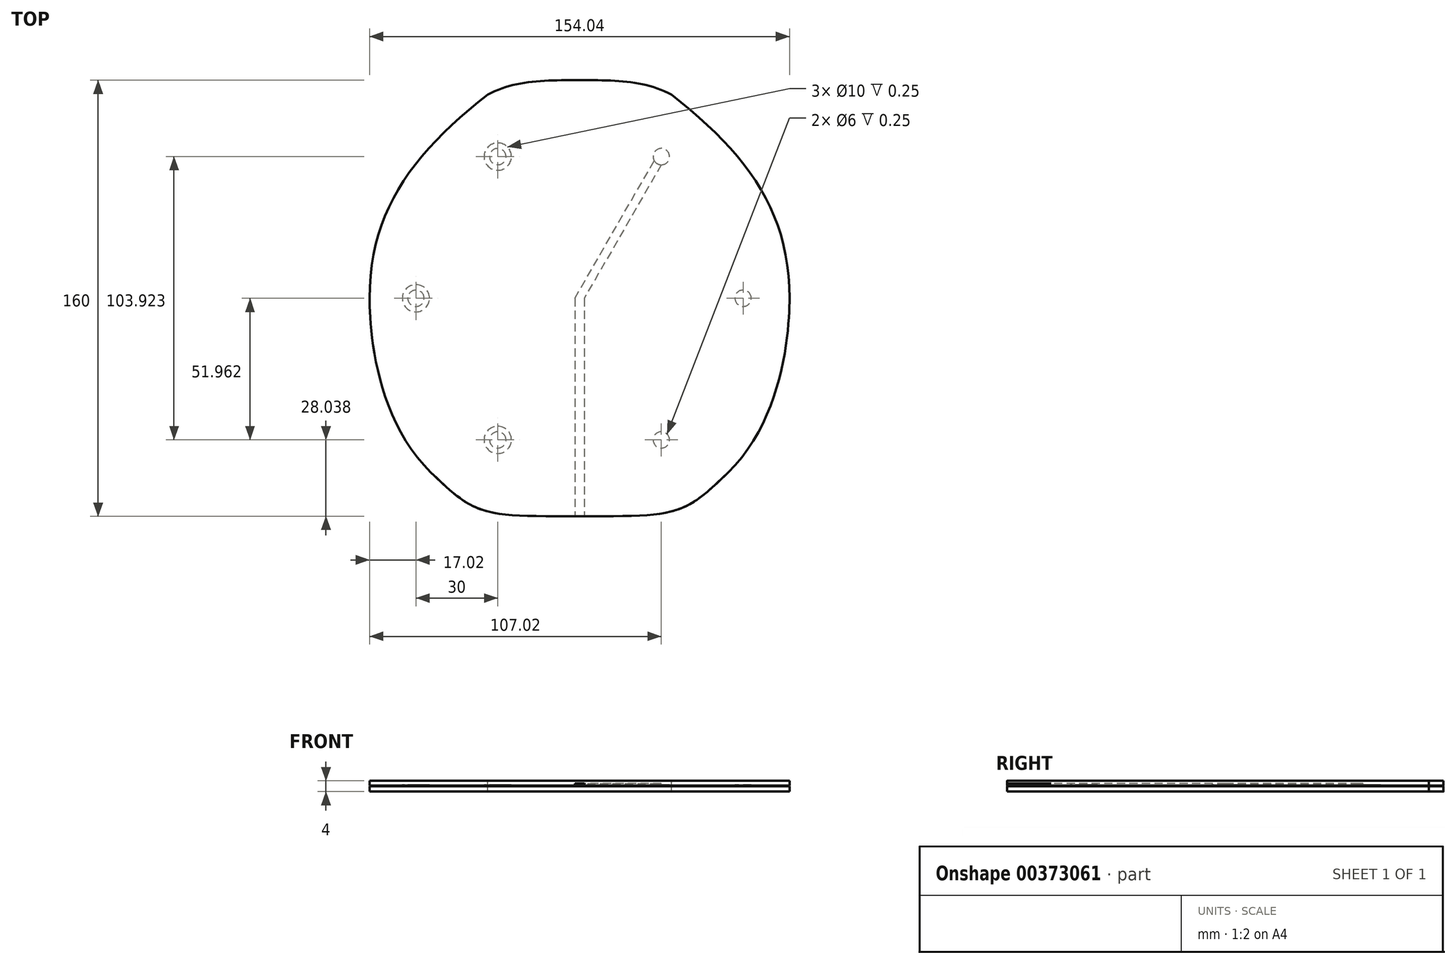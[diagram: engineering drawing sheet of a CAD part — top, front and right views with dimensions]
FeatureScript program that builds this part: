
annotation { "Feature Type Name" : "Feature", "Feature Type Description" : "" }
export const myFeature = defineFeature(function(context is Context, id is Id, definition is map)
    precondition{}
    {
        {
            assignVariable(context, id + "F0", {"name" : "spacer_thickness", "anyValue" : 2});
        }
        {
            var Q0;
            Q0=qCreatedBy(makeId("Top.planeOp"),FACE);
            var sketch = newSketch(context, id + "F1", { "sketchPlane" : qUnion([Q0])});
            skLineSegment(sketch, "E0", {"start": v(0, 80) * mm, "end": v(0, -80) * mm, "construction": true});
            skLineSegment(sketch, "E1", {"start": v(-77.02, 0) * mm, "end": v(77.02, 0) * mm, "construction": true});
            skFitSpline(sketch, "E2", {"points": [v(0, -80) * mm, v(-54.47, -63.95) * mm], "startDerivative": vector(-107.49, 0) * mm, "endDerivative": vector(-49.64, 48.15) * mm});
            skFitSpline(sketch, "E3", {"points": [v(-54.47, -63.95) * mm, v(-77.02, 0) * mm], "startDerivative": vector(-62.84, 60.95) * mm, "endDerivative": vector(0, 29.3) * mm});
            skFitSpline(sketch, "E4", {"points": [v(-77.02, 0) * mm, v(-33.74, 74.65) * mm], "startDerivative": vector(0, 97.25) * mm, "endDerivative": vector(81.5, 63.98) * mm});
            skFitSpline(sketch, "E5", {"points": [v(-33.74, 74.65) * mm, v(0, 80) * mm], "startDerivative": vector(30.02, 16.04) * mm, "endDerivative": vector(39.73, 0) * mm});
            skFitSpline(sketch, "E6.MirrorCS", {"points": [v(33.74, 74.65) * mm, v(0, 80) * mm], "startDerivative": vector(-30.02, 16.04) * mm, "endDerivative": vector(-39.73, 0) * mm});
            skFitSpline(sketch, "E7.MirrorCS", {"points": [v(77.02, 0) * mm, v(33.74, 74.65) * mm], "startDerivative": vector(0, 97.25) * mm, "endDerivative": vector(-81.5, 63.98) * mm});
            skFitSpline(sketch, "E8.MirrorCS", {"points": [v(54.47, -63.95) * mm, v(77.02, 0) * mm], "startDerivative": vector(62.84, 60.95) * mm, "endDerivative": vector(0, 29.3) * mm});
            skFitSpline(sketch, "E9.MirrorCS", {"points": [v(0, -80) * mm, v(54.47, -63.95) * mm], "startDerivative": vector(107.49, 0) * mm, "endDerivative": vector(49.64, 48.15) * mm});
            skSolve(sketch);
        }
        {
            var Q0;
            Q0=makeQuery(id+"F1.imprint","IMPRINT",FACE,{"disambiguationData":[TD([[makeQuery(id+"F1.imprint","IMPRINT",EDGE,{"derivedFrom":sQuery(id+"F1.wireOp",EDGE,"E2")}),-1.0]])]});
            extrude(context, id + "F2", {"entities" : qUnion([Q0]), "depth" : (getVariable(context, 'spacer_thickness')) * mm});
        }
        {
            assignVariable(context, id + "F3", {"name" : "wire_channel", "anyValue" : 1});
        }
        {
            assignVariable(context, id + "F4", {"name" : "piezo_thickness", "anyValue" : 0.5});
        }
        {
            assignVariable(context, id + "F5", {"name" : "piezo_plate_thickness", "anyValue" : 0.25});
        }
        {
            assignVariable(context, id + "F6", {"name" : "spacer_bottom_thickness", "anyValue" : 2});
        }
        {
            var Q0;
            Q0=makeQuery(id+"F2.opExtrude","CAP_FACE",FACE,{"disambiguationData":[OSD([sQuery(id+"F1.wireOp",EDGE,"E2"),sQuery(id+"F1.wireOp",EDGE,"E3"),sQuery(id+"F1.wireOp",EDGE,"E4"),sQuery(id+"F1.wireOp",EDGE,"E5"),sQuery(id+"F1.wireOp",EDGE,"E6.MirrorCS"),sQuery(id+"F1.wireOp",EDGE,"E7.MirrorCS"),sQuery(id+"F1.wireOp",EDGE,"E8.MirrorCS"),sQuery(id+"F1.wireOp",EDGE,"E9.MirrorCS")])],"isStart":false});
            var sketch = newSketch(context, id + "F7", { "sketchPlane" : qUnion([Q0])});
            skCircle(sketch, "E10", {"center": v(30, 51.96) * mm, "radius": 5 * mm});
            skCircle(sketch, "E11", {"center": v(60, 0) * mm, "radius": 5 * mm});
            skCircle(sketch, "E12", {"center": v(30, -51.96) * mm, "radius": 5 * mm});
            skCircle(sketch, "E13", {"center": v(0, 0) * mm, "radius": 60 * mm, "construction": true});
            skLineSegment(sketch, "E14", {"start": v(-119.63, 0) * mm, "end": v(92.07, 0) * mm, "construction": true});
            skLineSegment(sketch, "E15", {"start": v(0, 0) * mm, "end": v(44.3, 76.73) * mm, "construction": true});
            skCircle(sketch, "E16.MirrorC", {"center": v(-30, 51.96) * mm, "radius": 5 * mm});
            skCircle(sketch, "E17.MirrorC", {"center": v(-60, 0) * mm, "radius": 5 * mm});
            skCircle(sketch, "E18.MirrorC", {"center": v(-30, -51.96) * mm, "radius": 5 * mm});
            skCircle(sketch, "E19", {"center": v(30, 51.96) * mm, "radius": 3 * mm});
            skCircle(sketch, "E20", {"center": v(60, 0) * mm, "radius": 3 * mm});
            skCircle(sketch, "E21", {"center": v(30, -51.96) * mm, "radius": 3 * mm});
            skCircle(sketch, "E22.MirrorC", {"center": v(-60, 0) * mm, "radius": 3 * mm});
            skCircle(sketch, "E23.MirrorC", {"center": v(-30, 51.96) * mm, "radius": 3 * mm});
            skCircle(sketch, "E24.MirrorC", {"center": v(-30, -51.96) * mm, "radius": 3 * mm});
            skLineSegment(sketch, "E25", {"start": v(-1.73, 0) * mm, "end": v(28.2, 51.83) * mm});
            skLineSegment(sketch, "E26", {"start": v(29.56, 52.2) * mm, "end": v(30.42, 51.7) * mm});
            skLineSegment(sketch, "E27", {"start": v(30.79, 50.33) * mm, "end": v(1.73, 0) * mm});
            skLineSegment(sketch, "E28.bottom", {"start": v(-1.73, 0) * mm, "end": v(1.73, 0) * mm});
            skLineSegment(sketch, "E28.top", {"start": v(-1.73, -80) * mm, "end": v(1.73, -80) * mm});
            skLineSegment(sketch, "E28.left", {"start": v(-1.73, 0) * mm, "end": v(-1.73, -80) * mm});
            skLineSegment(sketch, "E28.right", {"start": v(1.73, 0) * mm, "end": v(1.73, -80) * mm});
            skPoint(sketch, "E29.visualSharp", {"position": v(28.7, 52.7) * mm});
            skArc(sketch, "E29.filletArc", {"start": v(29.56, 52.2) * mm, "mid": v(28.8, 52.3) * mm, "end": v(28.2, 51.83) * mm});
            skPoint(sketch, "E30.visualSharp", {"position": v(31.29, 51.2) * mm});
            skArc(sketch, "E30.filletArc", {"start": v(30.79, 50.33) * mm, "mid": v(30.89, 51.09) * mm, "end": v(30.42, 51.7) * mm});
            skSolve(sketch);
        }
        {
            var Q0;
            Q0=makeQuery(id+"F7.imprint","IMPRINT",FACE,{"disambiguationData":[TD([[makeQuery(id+"F7.imprint","IMPRINT",EDGE,{"derivedFrom":sQuery(id+"F7.wireOp",EDGE,"E10")}),1.0]])]});
            var Q1;
            Q1=makeQuery(id+"F7.imprint","IMPRINT",FACE,{"disambiguationData":[TD([[makeQuery(id+"F7.imprint","IMPRINT",EDGE,{"derivedFrom":sQuery(id+"F7.wireOp",EDGE,"E19")}),1.0]])]});
            var Q2;
            Q2=makeQuery(id+"F7.imprint","IMPRINT",FACE,{"disambiguationData":[TD([[makeQuery(id+"F7.imprint","IMPRINT",EDGE,{"derivedFrom":sQuery(id+"F7.wireOp",EDGE,"E11")}),1.0]])]});
            var Q3;
            Q3=makeQuery(id+"F7.imprint","IMPRINT",FACE,{"disambiguationData":[TD([[makeQuery(id+"F7.imprint","IMPRINT",EDGE,{"derivedFrom":sQuery(id+"F7.wireOp",EDGE,"E20")}),1.0]])]});
            var Q4;
            Q4=makeQuery(id+"F7.imprint","IMPRINT",FACE,{"disambiguationData":[TD([[makeQuery(id+"F7.imprint","IMPRINT",EDGE,{"derivedFrom":sQuery(id+"F7.wireOp",EDGE,"E12")}),1.0]])]});
            var Q5;
            Q5=makeQuery(id+"F7.imprint","IMPRINT",FACE,{"disambiguationData":[TD([[makeQuery(id+"F7.imprint","IMPRINT",EDGE,{"derivedFrom":sQuery(id+"F7.wireOp",EDGE,"E21")}),1.0]])]});
            var Q6;
            Q6=makeQuery(id+"F7.imprint","IMPRINT",FACE,{"disambiguationData":[TD([[makeQuery(id+"F7.imprint","IMPRINT",EDGE,{"derivedFrom":sQuery(id+"F7.wireOp",EDGE,"E18.MirrorC")}),-1.0]])]});
            var Q7;
            Q7=makeQuery(id+"F7.imprint","IMPRINT",FACE,{"disambiguationData":[TD([[makeQuery(id+"F7.imprint","IMPRINT",EDGE,{"derivedFrom":sQuery(id+"F7.wireOp",EDGE,"E24.MirrorC")}),-1.0]])]});
            var Q8;
            Q8=makeQuery(id+"F7.imprint","IMPRINT",FACE,{"disambiguationData":[TD([[makeQuery(id+"F7.imprint","IMPRINT",EDGE,{"derivedFrom":sQuery(id+"F7.wireOp",EDGE,"E17.MirrorC")}),-1.0]])]});
            var Q9;
            Q9=makeQuery(id+"F7.imprint","IMPRINT",FACE,{"disambiguationData":[TD([[makeQuery(id+"F7.imprint","IMPRINT",EDGE,{"derivedFrom":sQuery(id+"F7.wireOp",EDGE,"E22.MirrorC")}),-1.0]])]});
            var Q10;
            Q10=makeQuery(id+"F7.imprint","IMPRINT",FACE,{"disambiguationData":[TD([[makeQuery(id+"F7.imprint","IMPRINT",EDGE,{"derivedFrom":sQuery(id+"F7.wireOp",EDGE,"E16.MirrorC")}),-1.0]])]});
            var Q11;
            Q11=makeQuery(id+"F7.imprint","IMPRINT",FACE,{"disambiguationData":[TD([[makeQuery(id+"F7.imprint","IMPRINT",EDGE,{"derivedFrom":sQuery(id+"F7.wireOp",EDGE,"E23.MirrorC")}),-1.0]])]});
            var Q12;
            Q12=makeQuery(id+"F7.imprint","IMPRINT",FACE,{"disambiguationData":[TD([[makeQuery(id+"F7.imprint","IMPRINT",EDGE,{"derivedFrom":sQuery(id+"F7.wireOp",EDGE,"E19")}),-1.0]])]});
            var Q13;
            Q13=makeQuery(id+"F2.opExtrude","SWEPT_BODY",BODY,{"disambiguationData":[OSD([sQuery(id+"F1.wireOp",EDGE,"E2"),sQuery(id+"F1.wireOp",EDGE,"E3"),sQuery(id+"F1.wireOp",EDGE,"E4"),sQuery(id+"F1.wireOp",EDGE,"E5"),sQuery(id+"F1.wireOp",EDGE,"E6.MirrorCS"),sQuery(id+"F1.wireOp",EDGE,"E7.MirrorCS"),sQuery(id+"F1.wireOp",EDGE,"E8.MirrorCS"),sQuery(id+"F1.wireOp",EDGE,"E9.MirrorCS")])]});
            extrude(context, id + "F8", {"entities" : qUnion([Q0, Q1, Q2, Q3, Q4, Q5, Q6, Q7, Q8, Q9, Q10, Q11, Q12]), "operationType" : NewBodyOperationType.REMOVE, "oppositeDirection" : true, "endBoundEntityBody" : qUnion([Q13]), "depth" : (getVariable(context, 'spacer_thickness')) * mm});
        }
        {
            var Q0;
            Q0=makeQuery(id+"F7.imprint","IMPRINT",FACE,{"disambiguationData":[TD([[makeQuery(id+"F7.imprint","IMPRINT",EDGE,{"derivedFrom":sQuery(id+"F7.wireOp",EDGE,"E10")}),1.0]])]});
            var Q1;
            Q1=makeQuery(id+"F7.imprint","IMPRINT",FACE,{"disambiguationData":[TD([[makeQuery(id+"F7.imprint","IMPRINT",EDGE,{"derivedFrom":sQuery(id+"F7.wireOp",EDGE,"E11")}),1.0]])]});
            var Q2;
            Q2=makeQuery(id+"F7.imprint","IMPRINT",FACE,{"disambiguationData":[TD([[makeQuery(id+"F7.imprint","IMPRINT",EDGE,{"derivedFrom":sQuery(id+"F7.wireOp",EDGE,"E12")}),1.0]])]});
            var Q3;
            Q3=makeQuery(id+"F7.imprint","IMPRINT",FACE,{"disambiguationData":[TD([[makeQuery(id+"F7.imprint","IMPRINT",EDGE,{"derivedFrom":sQuery(id+"F7.wireOp",EDGE,"E18.MirrorC")}),-1.0]])]});
            var Q4;
            Q4=makeQuery(id+"F7.imprint","IMPRINT",FACE,{"disambiguationData":[TD([[makeQuery(id+"F7.imprint","IMPRINT",EDGE,{"derivedFrom":sQuery(id+"F7.wireOp",EDGE,"E17.MirrorC")}),-1.0]])]});
            var Q5;
            Q5=makeQuery(id+"F7.imprint","IMPRINT",FACE,{"disambiguationData":[TD([[makeQuery(id+"F7.imprint","IMPRINT",EDGE,{"derivedFrom":sQuery(id+"F7.wireOp",EDGE,"E16.MirrorC")}),-1.0]])]});
            var Q6;
            Q6=makeQuery(id+"F7.imprint","IMPRINT",FACE,{"disambiguationData":[TD([[makeQuery(id+"F7.imprint","IMPRINT",EDGE,{"derivedFrom":sQuery(id+"F7.wireOp",EDGE,"E19")}),-1.0]])]});
            extrude(context, id + "F9", {"entities" : qUnion([Q0, Q1, Q2, Q3, Q4, Q5, Q6]), "operationType" : NewBodyOperationType.ADD, "oppositeDirection" : true, "depth" : (getVariable(context, 'spacer_thickness') - getVariable(context, 'piezo_plate_thickness')) * mm});
        }
        {
            var Q0;
            Q0=makeQuery(id+"F7.imprint","IMPRINT",FACE,{"disambiguationData":[TD([[makeQuery(id+"F7.imprint","IMPRINT",EDGE,{"derivedFrom":sQuery(id+"F7.wireOp",EDGE,"E19")}),1.0]])]});
            var Q1;
            Q1=makeQuery(id+"F7.imprint","IMPRINT",FACE,{"disambiguationData":[TD([[makeQuery(id+"F7.imprint","IMPRINT",EDGE,{"derivedFrom":sQuery(id+"F7.wireOp",EDGE,"E20")}),1.0]])]});
            var Q2;
            Q2=makeQuery(id+"F7.imprint","IMPRINT",FACE,{"disambiguationData":[TD([[makeQuery(id+"F7.imprint","IMPRINT",EDGE,{"derivedFrom":sQuery(id+"F7.wireOp",EDGE,"E21")}),1.0]])]});
            var Q3;
            Q3=makeQuery(id+"F7.imprint","IMPRINT",FACE,{"disambiguationData":[TD([[makeQuery(id+"F7.imprint","IMPRINT",EDGE,{"derivedFrom":sQuery(id+"F7.wireOp",EDGE,"E24.MirrorC")}),-1.0]])]});
            var Q4;
            Q4=makeQuery(id+"F7.imprint","IMPRINT",FACE,{"disambiguationData":[TD([[makeQuery(id+"F7.imprint","IMPRINT",EDGE,{"derivedFrom":sQuery(id+"F7.wireOp",EDGE,"E22.MirrorC")}),-1.0]])]});
            var Q5;
            Q5=makeQuery(id+"F7.imprint","IMPRINT",FACE,{"disambiguationData":[TD([[makeQuery(id+"F7.imprint","IMPRINT",EDGE,{"derivedFrom":sQuery(id+"F7.wireOp",EDGE,"E23.MirrorC")}),-1.0]])]});
            extrude(context, id + "F10", {"entities" : qUnion([Q0, Q1, Q2, Q3, Q4, Q5]), "operationType" : NewBodyOperationType.ADD, "oppositeDirection" : true, "depth" : (getVariable(context, 'spacer_thickness') - getVariable(context, 'piezo_thickness')) * mm});
        }
        {
            var Q0;
            {var subQ1=sQuery(id+"F7.wireOp",EDGE,"E25");Q0=makeQuery(id+"F7.imprint","IMPRINT",FACE,{"disambiguationData":[TD([[makeQuery(id+"F7.imprint","IMPRINT",EDGE,{"derivedFrom":subQ1}),-1.0]])]});}
            extrude(context, id + "F11", {"entities" : qUnion([Q0]), "operationType" : NewBodyOperationType.REMOVE, "oppositeDirection" : true, "depth" : 5 * mm});
        }
        {
            var Q0;
            {var subQ1=sQuery(id+"F7.wireOp",EDGE,"E25");Q0=makeQuery(id+"F7.imprint","IMPRINT",FACE,{"disambiguationData":[TD([[makeQuery(id+"F7.imprint","IMPRINT",EDGE,{"derivedFrom":subQ1}),-1.0]])]});}
            extrude(context, id + "F12", {"entities" : qUnion([Q0]), "operationType" : NewBodyOperationType.ADD, "oppositeDirection" : true, "depth" : (getVariable(context, 'spacer_thickness') - getVariable(context, 'wire_channel')) * mm});
        }
        {
            var Q0;
            Q0=makeQuery(id+"F7.imprint","IMPRINT",FACE,{"disambiguationData":[TD([[makeQuery(id+"F7.imprint","IMPRINT",EDGE,{"derivedFrom":sQuery(id+"F7.wireOp",EDGE,"E28.bottom")}),-1.0]])]});
            extrude(context, id + "F13", {"entities" : qUnion([Q0]), "operationType" : NewBodyOperationType.REMOVE, "oppositeDirection" : true, "depth" : 5 * mm});
        }
        {
            var Q0;
            Q0=makeQuery(id+"F7.imprint","IMPRINT",FACE,{"disambiguationData":[TD([[makeQuery(id+"F7.imprint","IMPRINT",EDGE,{"derivedFrom":sQuery(id+"F7.wireOp",EDGE,"E28.bottom")}),-1.0]])]});
            extrude(context, id + "F14", {"entities" : qUnion([Q0]), "operationType" : NewBodyOperationType.ADD, "oppositeDirection" : true, "depth" : (getVariable(context, 'spacer_thickness') - getVariable(context, 'wire_channel')) * mm});
        }
        {
            var Q0;
            Q0 = qSketchRegion(id + "F1", true);
            extrude(context, id + "F15", {"entities" : qUnion([Q0]), "oppositeDirection" : true, "depth" : (getVariable(context, 'spacer_bottom_thickness')) * mm});
        }
    });
